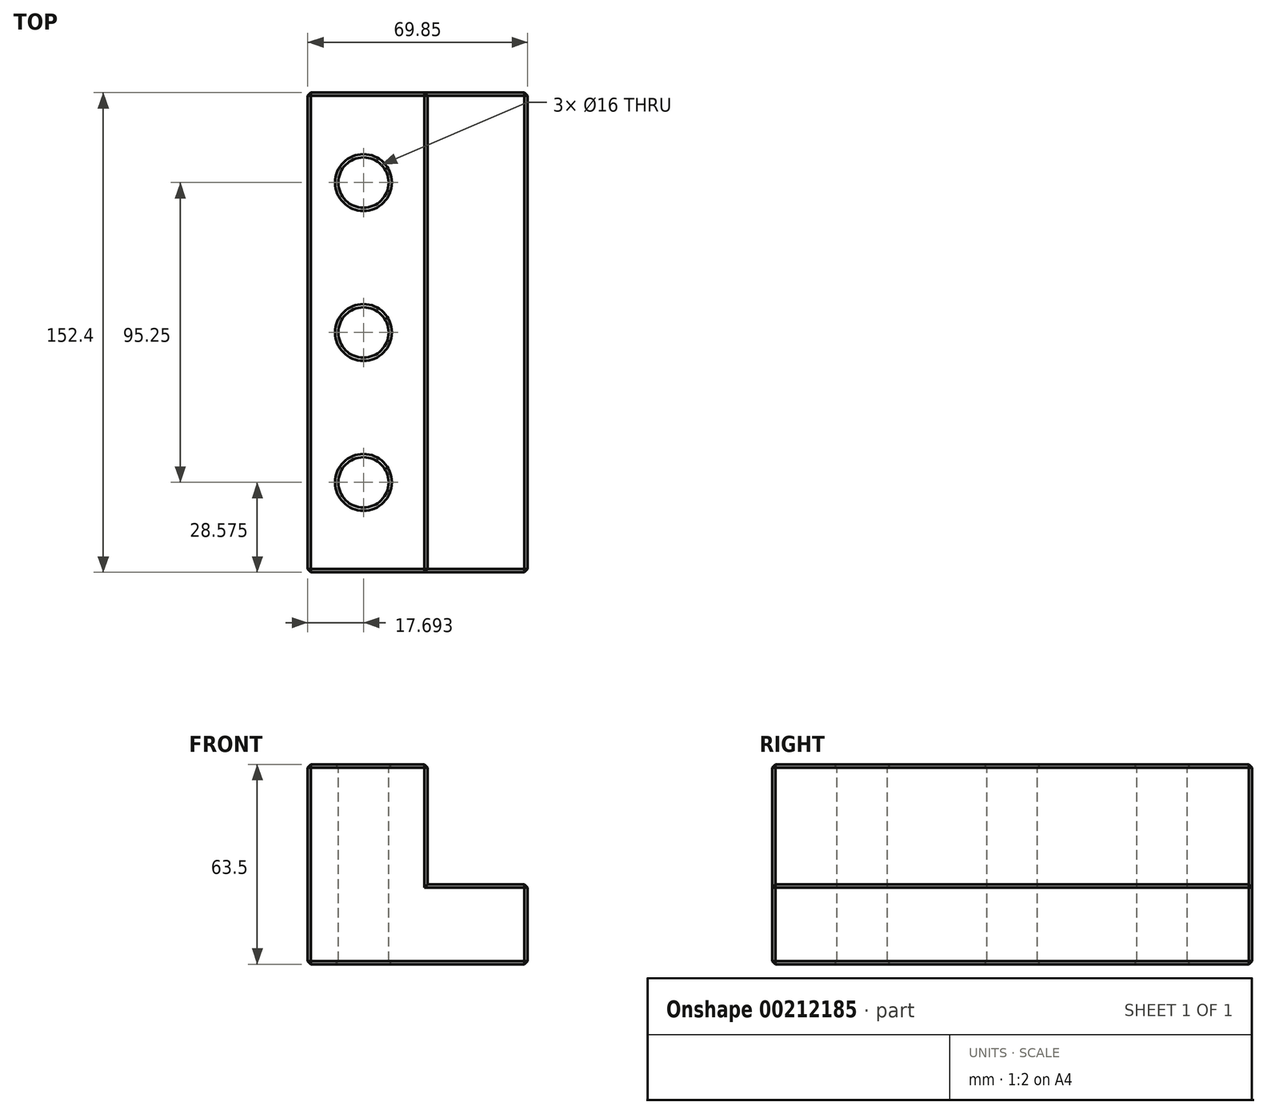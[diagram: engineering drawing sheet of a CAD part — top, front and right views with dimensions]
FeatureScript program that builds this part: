
annotation { "Feature Type Name" : "Feature", "Feature Type Description" : "" }
export const myFeature = defineFeature(function(context is Context, id is Id, definition is map)
    precondition{}
    {
        {
            var Q0;
            Q0=qCreatedBy(makeId("Front.planeOp"),FACE);
            var sketch = newSketch(context, id + "F0", { "sketchPlane" : qUnion([Q0])});
            skLineSegment(sketch, "E0", {"start": v(0, 0) * mm, "end": v(0, 63.5) * mm});
            skLineSegment(sketch, "E1", {"start": v(0, 63.5) * mm, "end": v(38.1, 63.5) * mm});
            skLineSegment(sketch, "E2", {"start": v(38.1, 63.5) * mm, "end": v(38.1, 25.4) * mm});
            skLineSegment(sketch, "E3", {"start": v(38.1, 25.4) * mm, "end": v(69.85, 25.4) * mm});
            skLineSegment(sketch, "E4", {"start": v(69.85, 25.4) * mm, "end": v(69.85, 0) * mm});
            skLineSegment(sketch, "E5", {"start": v(69.85, 0) * mm, "end": v(0, 0) * mm});
            skSolve(sketch);
        }
        {
            var Q0;
            Q0=makeQuery(id+"F0.imprint","IMPRINT",FACE,{"disambiguationData":[TD([[makeQuery(id+"F0.imprint","IMPRINT",EDGE,{"derivedFrom":sQuery(id+"F0.wireOp",EDGE,"E0")}),-1.0]])]});
            extrude(context, id + "F1", {"entities" : qUnion([Q0]), "depth" : 152.4 * mm});
        }
        {
            var Q0;
            Q0=makeQuery(id+"F1.opExtrude","SWEPT_FACE",FACE,{"disambiguationData":[OSD([sQuery(id+"F0.wireOp",EDGE,"E1")])]});
            var sketch = newSketch(context, id + "F2", { "sketchPlane" : qUnion([Q0])});
            skCircle(sketch, "E6", {"center": v(17.7, -28.58) * mm, "radius": 8 * mm});
            skCircle(sketch, "E7", {"center": v(17.7, -76.2) * mm, "radius": 8 * mm});
            skCircle(sketch, "E8", {"center": v(17.7, -123.83) * mm, "radius": 8 * mm});
            skSolve(sketch);
        }
        {
            var Q0;
            Q0=makeQuery(id+"F2.imprint","IMPRINT",FACE,{"disambiguationData":[TD([[makeQuery(id+"F2.imprint","IMPRINT",EDGE,{"derivedFrom":sQuery(id+"F2.wireOp",EDGE,"E6")}),1.0]])]});
            var Q1;
            Q1=makeQuery(id+"F2.imprint","IMPRINT",FACE,{"disambiguationData":[TD([[makeQuery(id+"F2.imprint","IMPRINT",EDGE,{"derivedFrom":sQuery(id+"F2.wireOp",EDGE,"E7")}),1.0]])]});
            var Q2;
            Q2=makeQuery(id+"F2.imprint","IMPRINT",FACE,{"disambiguationData":[TD([[makeQuery(id+"F2.imprint","IMPRINT",EDGE,{"derivedFrom":sQuery(id+"F2.wireOp",EDGE,"E8")}),1.0]])]});
            extrude(context, id + "F3", {"entities" : qUnion([Q0, Q1, Q2]), "operationType" : NewBodyOperationType.REMOVE, "endBound" : BoundingType.THROUGH_ALL, "oppositeDirection" : true, "depth" : 25.4 * mm});
        }
        {
            var Q0;
            Q0=makeQuery(id+"F1.opExtrude","CAP_FACE",FACE,{"disambiguationData":[OSD([sQuery(id+"F0.wireOp",EDGE,"E0"),sQuery(id+"F0.wireOp",EDGE,"E1"),sQuery(id+"F0.wireOp",EDGE,"E2"),sQuery(id+"F0.wireOp",EDGE,"E3"),sQuery(id+"F0.wireOp",EDGE,"E4"),sQuery(id+"F0.wireOp",EDGE,"E5")])],"isStart":false});
            var Q1;
            Q1=makeQuery(id+"F1.opExtrude","CAP_FACE",FACE,{"disambiguationData":[OSD([sQuery(id+"F0.wireOp",EDGE,"E0"),sQuery(id+"F0.wireOp",EDGE,"E1"),sQuery(id+"F0.wireOp",EDGE,"E2"),sQuery(id+"F0.wireOp",EDGE,"E3"),sQuery(id+"F0.wireOp",EDGE,"E4"),sQuery(id+"F0.wireOp",EDGE,"E5")])],"isStart":true});
            var Q2;
            Q2=makeQuery(id+"F1.opExtrude","SWEPT_FACE",FACE,{"disambiguationData":[OSD([sQuery(id+"F0.wireOp",EDGE,"E1")])]});
            var Q3;
            Q3=makeQuery(id+"F1.opExtrude","SWEPT_FACE",FACE,{"disambiguationData":[OSD([sQuery(id+"F0.wireOp",EDGE,"E4")])]});
            var Q4;
            Q4=makeQuery(id+"F1.opExtrude","SWEPT_EDGE",EDGE,{"disambiguationData":[OSD([sQuery(id+"F0.wireOp",EDGE,"E0"),sQuery(id+"F0.wireOp",EDGE,"E5")])]});
            var Q5;
            Q5=makeQuery(id+"F3.boolean.opBoolean","INTERSECT",EDGE,{"derivedFrom":[makeQuery(id+"F1.opExtrude","SWEPT_FACE",FACE,{"disambiguationData":[OSD([sQuery(id+"F0.wireOp",EDGE,"E5")])]}),makeQuery(id+"F3.opExtrude","SWEPT_FACE",FACE,{"disambiguationData":[OSD([sQuery(id+"F2.wireOp",EDGE,"E8")])]})]});
            var Q6;
            Q6=makeQuery(id+"F3.boolean.opBoolean","INTERSECT",EDGE,{"derivedFrom":[makeQuery(id+"F1.opExtrude","SWEPT_FACE",FACE,{"disambiguationData":[OSD([sQuery(id+"F0.wireOp",EDGE,"E5")])]}),makeQuery(id+"F3.opExtrude","SWEPT_FACE",FACE,{"disambiguationData":[OSD([sQuery(id+"F2.wireOp",EDGE,"E7")])]})]});
            var Q7;
            Q7=makeQuery(id+"F3.boolean.opBoolean","INTERSECT",EDGE,{"derivedFrom":[makeQuery(id+"F1.opExtrude","SWEPT_FACE",FACE,{"disambiguationData":[OSD([sQuery(id+"F0.wireOp",EDGE,"E5")])]}),makeQuery(id+"F3.opExtrude","SWEPT_FACE",FACE,{"disambiguationData":[OSD([sQuery(id+"F2.wireOp",EDGE,"E6")])]})]});
            chamfer(context, id + "F4", {"entities" : qUnion([Q0, Q1, Q2, Q3, Q4, Q5, Q6, Q7]), "width" : 1.02 * mm, "tangentPropagation" : true});
        }
    });
